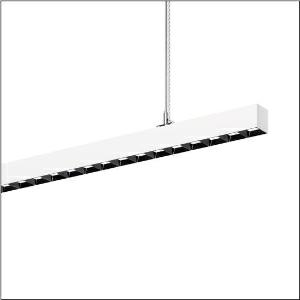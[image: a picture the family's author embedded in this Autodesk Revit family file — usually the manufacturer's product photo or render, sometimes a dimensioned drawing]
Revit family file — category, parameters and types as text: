
# Revit family: silica_r__21_51mx34dc3dwb_cbfc
name_source: partatom
category: Lighting Fixtures
units: mm (PartAtom-declared; Revit-internal decimal feet)

## family parameters
Cut with Voids When Loaded = No
Host = Face
Light Source = No
Part Type = Normal
Room Calculation Point = No
Round Connector Dimension = Use Diameter
Shared = No

## types (1)
- --- (1 x LED, 19200 lm, 129.1 W, 3000K)
    Apparent Load = 129 VA
    CIE Flux Codes = 74 94 99 56 100
    Color Rendering = 80
    Color Temperature = 3000K
    Default Elevation = 1800 mm
    Description = Silica® 21, office luminaire, primary light control with darklight reflector, of PMMA, black, light emission: direct/indirect distribution, primary light characteristic: asymmetric, installation type: suspended mounting, LED, rated luminous flux: 19.200lm, luminous efficacy: 149lm/W, light colour: 830, colour temperature: 3000K, with terminal, 3+2-pole, max. 2.5mm², mains connection: 220..240V, AC, 50/60Hz, rated input power: 129.1W, luminaire housing, of aluminium, traffic white (RAL 9016), length: 3.004mm, width: 53mm, height: 53mm, protection rating (complete): IP20, insulation class (complete): insulation class I (protective earthing), certification: CE, permissible operating ambient temperature: 0..+35°C, standard: EN 50419, packaging unit: 1 piece
    Height = 53 mm
    Lamp = 1 x LED
    Lamp Light Flux = 19200 lm
    Lamp Power = 129.1 W
    Lamp count = 1
    Length = 3004 mm
    Luminous efficacy = 149 lm/W
    Manufacturer = Siteco
    ModVariant = No
    Model = 51MX34DC3DWB
    Mounting Place = Ceiling
    Mounting Type = Pendant
    Number of Poles = 1
    OnlyDefault = Yes
    Power Factor = 1
    Product Name = Silica® 21
    Product group = office luminaire | ceiling pendant
    ProductGroupID = 902
    Protection Class = Protection class I
    Protection Degree = IP 20
    RLX_Detail_Level = 1
    RLX_Emergency_Light_Flux = 0 lm
    RLX_Emergency_Type = 0
    RLX_Emergency_Type_DB = No
    RlxData = <blob elided: 65597 chars, md5=7dace1be>
    Socket = socket
    Standby Power = 0 W
    System Light Flux = 19200 lm
    System Power = 129 W
    Type Comments = factory setting: luminous flux: 100 % | dim-lin: 254 | 448 mA
    Type Image = l_1335871.jpg
    URL = http://relux.com
    VarID = @adj_089765
    Voltage = 0 V
    Weight = 0.00 kg
    Width = 53 mm

## geometry (parser evidence)
native form markers: Blend x4, Sweep x12
no freeform markers — native parametric forms only
